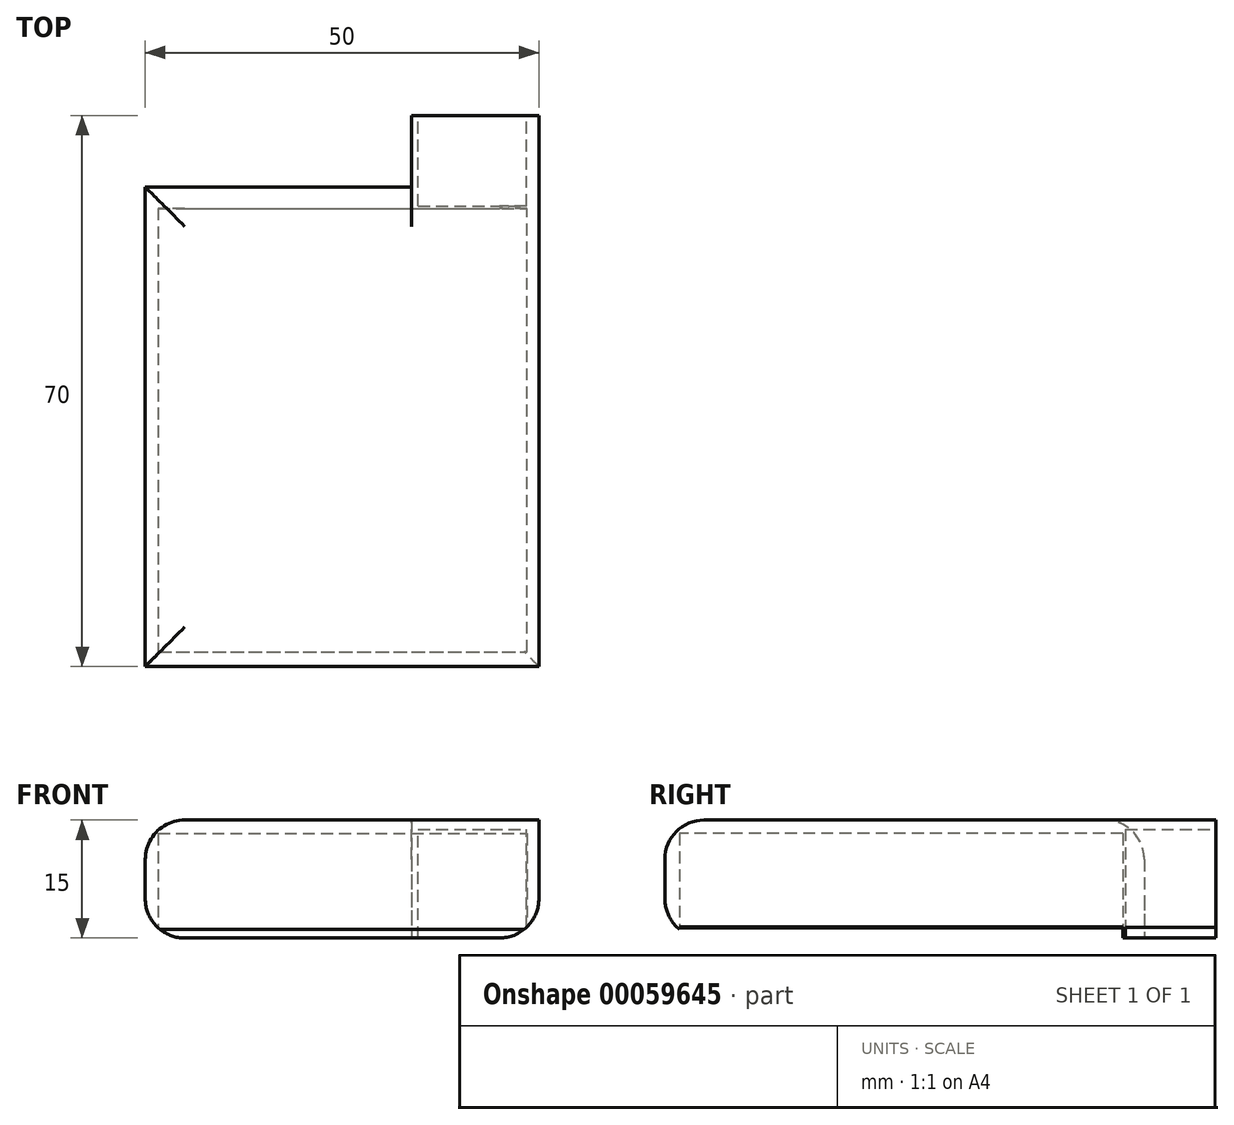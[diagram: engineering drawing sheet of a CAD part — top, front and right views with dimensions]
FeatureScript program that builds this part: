
annotation { "Feature Type Name" : "Feature", "Feature Type Description" : "" }
export const myFeature = defineFeature(function(context is Context, id is Id, definition is map)
    precondition{}
    {
        {
            var Q0;
            Q0=qCreatedBy(makeId("Top.planeOp"),FACE);
            var sketch = newSketch(context, id + "F0", { "sketchPlane" : qUnion([Q0])});
            skLineSegment(sketch, "E0.top", {"start": v(-57.37, 4.96) * mm, "end": v(-7.37, 4.96) * mm});
            skLineSegment(sketch, "E0.right", {"start": v(-7.37, 74.96) * mm, "end": v(-7.37, 4.96) * mm});
            skLineSegment(sketch, "E1", {"start": v(-23.51, 74.96) * mm, "end": v(-23.51, 65.87) * mm});
            skLineSegment(sketch, "E2", {"start": v(-23.51, 65.87) * mm, "end": v(-57.37, 65.87) * mm});
            skLineSegment(sketch, "E3", {"start": v(-23.51, 74.96) * mm, "end": v(-7.37, 74.96) * mm});
            skLineSegment(sketch, "E4", {"start": v(-57.37, 65.87) * mm, "end": v(-57.37, 4.96) * mm});
            skSolve(sketch);
        }
        {
            var Q0;
            Q0 = qSketchRegion(id + "F0", true);
            extrude(context, id + "F1", {"entities" : qUnion([Q0]), "depth" : 15 * mm});
        }
        {
            var Q0;
            Q0=qCreatedBy(makeId("Top.planeOp"),FACE);
            var sketch = newSketch(context, id + "F2", { "sketchPlane" : qUnion([Q0])});
            skLineSegment(sketch, "E5.bottom", {"start": v(-55.74, 63.15) * mm, "end": v(-8.87, 63.15) * mm});
            skLineSegment(sketch, "E5.top", {"start": v(-55.74, 6.83) * mm, "end": v(-8.87, 6.83) * mm});
            skLineSegment(sketch, "E5.left", {"start": v(-55.74, 63.15) * mm, "end": v(-55.74, 6.83) * mm});
            skLineSegment(sketch, "E5.right", {"start": v(-8.87, 63.15) * mm, "end": v(-8.87, 6.83) * mm});
            skSolve(sketch);
        }
        {
            var Q0;
            Q0 = qSketchRegion(id + "F2", true);
            extrude(context, id + "F3", {"entities" : qUnion([Q0]), "operationType" : NewBodyOperationType.REMOVE, "depth" : 13.3 * mm});
        }
        {
            var Q0;
            Q0=qCreatedBy(makeId("Top.planeOp"),FACE);
            var sketch = newSketch(context, id + "F4", { "sketchPlane" : qUnion([Q0])});
            skLineSegment(sketch, "E6.bottom", {"start": v(-22.7, 63.48) * mm, "end": v(-8.95, 63.48) * mm});
            skLineSegment(sketch, "E6.top", {"start": v(-22.7, 76.27) * mm, "end": v(-8.95, 76.27) * mm});
            skLineSegment(sketch, "E6.left", {"start": v(-22.7, 63.48) * mm, "end": v(-22.7, 76.27) * mm});
            skLineSegment(sketch, "E6.right", {"start": v(-8.95, 63.48) * mm, "end": v(-8.95, 76.27) * mm});
            skSolve(sketch);
        }
        {
            var Q0;
            Q0 = qSketchRegion(id + "F4", true);
            extrude(context, id + "F5", {"entities" : qUnion([Q0]), "operationType" : NewBodyOperationType.REMOVE, "depth" : 13.82 * mm});
        }
        {
            var Q0;
            Q0=makeQuery(id+"F1.opExtrude","CAP_EDGE",EDGE,{"disambiguationData":[OSD([sQuery(id+"F0.wireOp",EDGE,"E0.top")])],"isStart":false});
            var Q1;
            Q1=makeQuery(id+"F1.opExtrude","CAP_EDGE",EDGE,{"disambiguationData":[OSD([sQuery(id+"F0.wireOp",EDGE,"E4")])],"isStart":false});
            var Q2;
            Q2=makeQuery(id+"F1.opExtrude","CAP_EDGE",EDGE,{"disambiguationData":[OSD([sQuery(id+"F0.wireOp",EDGE,"E2")])],"isStart":false});
            var Q3;
            Q3=makeQuery(id+"F1.opExtrude","CAP_EDGE",EDGE,{"disambiguationData":[OSD([sQuery(id+"F0.wireOp",EDGE,"E4")])],"isStart":true});
            var Q4;
            Q4=makeQuery(id+"F1.opExtrude","CAP_EDGE",EDGE,{"disambiguationData":[OSD([sQuery(id+"F0.wireOp",EDGE,"E0.top")])],"isStart":true});
            var Q5;
            Q5=makeQuery(id+"F1.opExtrude","CAP_EDGE",EDGE,{"disambiguationData":[OSD([sQuery(id+"F0.wireOp",EDGE,"E0.right")])],"isStart":true});
            fillet(context, id + "F6", {"entities" : qUnion([Q0, Q1, Q2, Q3, Q4, Q5]), "radius" : 5 * mm, "tangentPropagation" : true, "allowEdgeOverflow" : false});
        }
    });
